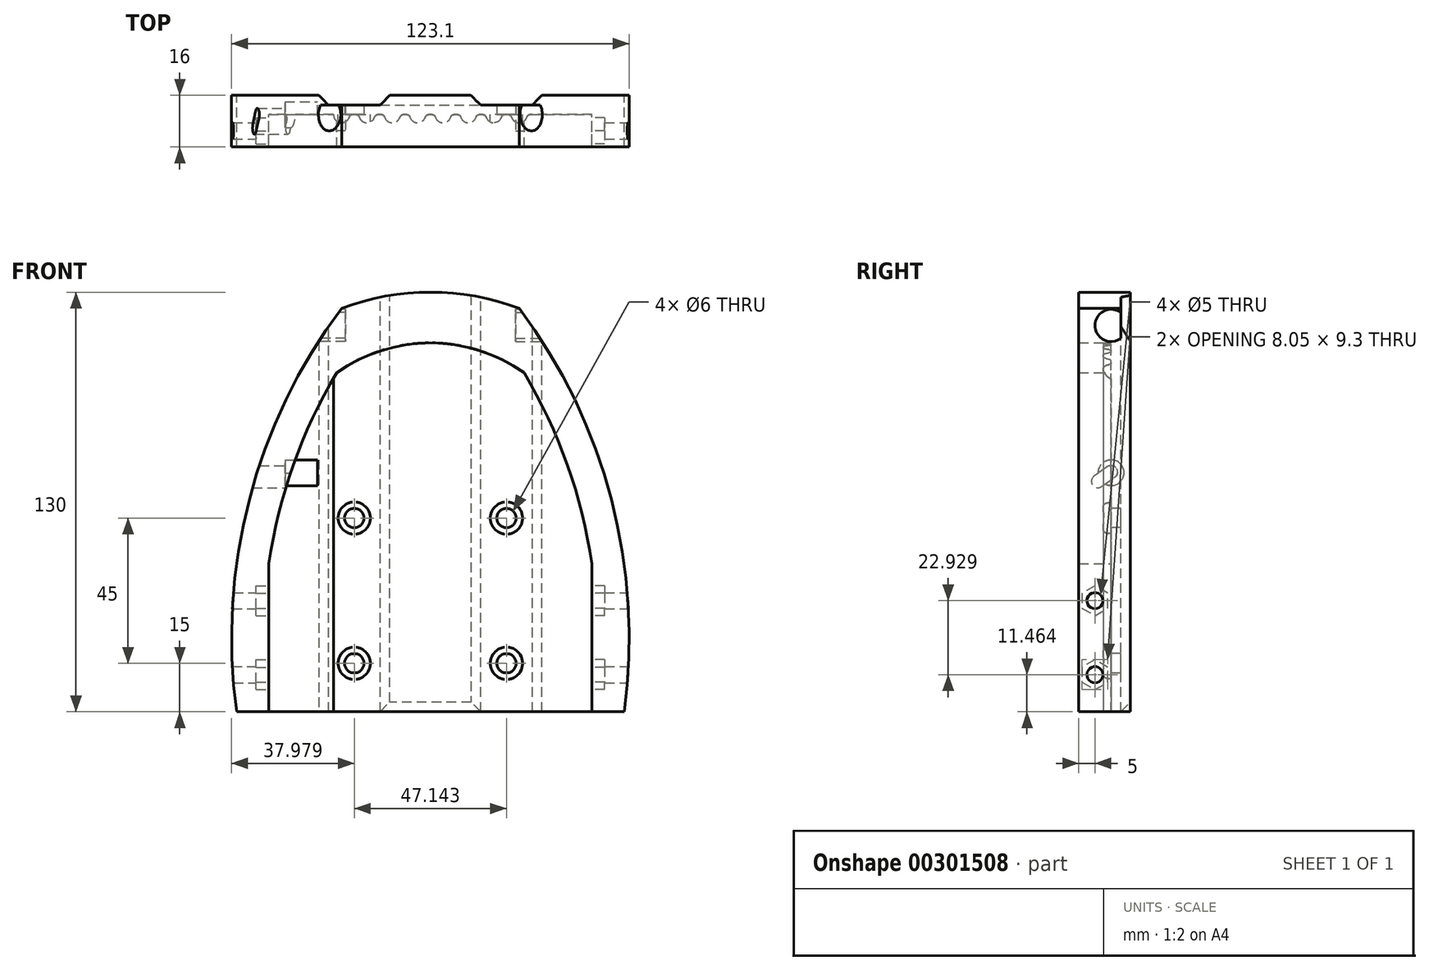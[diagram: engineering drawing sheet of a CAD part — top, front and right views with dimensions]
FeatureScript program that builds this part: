
annotation { "Feature Type Name" : "Feature", "Feature Type Description" : "" }
export const myFeature = defineFeature(function(context is Context, id is Id, definition is map)
    precondition{}
    {
        {
            var Q0;
            Q0=qCreatedBy(makeId("Front.planeOp"),FACE);
            var sketch = newSketch(context, id + "F0", { "sketchPlane" : qUnion([Q0])});
            skArc(sketch, "E0", {"start": v(-27.5, 125) * mm, "mid": v(-56.08, 65.7) * mm, "end": v(-60, 0) * mm});
            skArc(sketch, "E1", {"start": v(0, 130) * mm, "mid": v(-13.98, 128.74) * mm, "end": v(-27.5, 125) * mm});
            skLineSegment(sketch, "E2", {"start": v(-60, 0) * mm, "end": v(0, 0) * mm});
            skArc(sketch, "E3.MirrorCS", {"start": v(0, 130) * mm, "mid": v(13.98, 128.74) * mm, "end": v(27.5, 125) * mm});
            skArc(sketch, "E4.MirrorCS", {"start": v(27.5, 125) * mm, "mid": v(56.08, 65.7) * mm, "end": v(60, 0) * mm});
            skLineSegment(sketch, "E5.MirrorCS", {"start": v(60, 0) * mm, "end": v(0, 0) * mm});
            skSolve(sketch);
        }
        {
            var Q0;
            Q0=qSketchRegion(id+"F0",true);
            extrude(context, id + "F1", {"entities" : qUnion([Q0]), "depth" : 3 * mm});
        }
        {
            var Q0;
            Q0=makeQuery(id+"F1.opExtrude","CAP_FACE",FACE,{"disambiguationData":[OSD([sQuery(id+"F0.wireOp",EDGE,"E0"),sQuery(id+"F0.wireOp",EDGE,"E1"),sQuery(id+"F0.wireOp",EDGE,"E2"),sQuery(id+"F0.wireOp",EDGE,"E3.MirrorCS"),sQuery(id+"F0.wireOp",EDGE,"E4.MirrorCS"),sQuery(id+"F0.wireOp",EDGE,"E5.MirrorCS")])],"isStart":false});
            var sketch = newSketch(context, id + "F2", { "sketchPlane" : qUnion([Q0])});
            skArc(sketch, "E6", {"start": v(27.5, 125) * mm, "mid": v(0, 130) * mm, "end": v(-27.5, 125) * mm});
            skArc(sketch, "E7", {"start": v(-27.5, 125) * mm, "mid": v(-56.08, 65.7) * mm, "end": v(-60, 0) * mm});
            skArc(sketch, "E8", {"start": v(60, 0) * mm, "mid": v(56.08, 65.7) * mm, "end": v(27.5, 125) * mm});
            skArc(sketch, "E9", {"start": v(29.01, 105) * mm, "mid": v(0, 114.28) * mm, "end": v(-29.01, 105) * mm});
            skArc(sketch, "E10", {"start": v(-29.01, 105) * mm, "mid": v(-48.55, 54.3) * mm, "end": v(-50, 0) * mm});
            skArc(sketch, "E11", {"start": v(50, 0) * mm, "mid": v(48.55, 54.3) * mm, "end": v(29.01, 105) * mm});
            skLineSegment(sketch, "E12", {"start": v(-60, 0) * mm, "end": v(-50, 0) * mm});
            skLineSegment(sketch, "E13", {"start": v(50, 0) * mm, "end": v(60, 0) * mm});
            skLineSegment(sketch, "E14", {"start": v(-50, 45.86) * mm, "end": v(-50, 0) * mm});
            skPoint(sketch, "E15", {"position": v(-50, 43.93) * mm});
            skLineSegment(sketch, "E16.MirrorCS", {"start": v(50, 45.86) * mm, "end": v(50, 0) * mm});
            skSolve(sketch);
        }
        {
            var Q0;
            Q0=qSketchRegion(id+"F2",true);
            extrude(context, id + "F3", {"entities" : qUnion([Q0]), "operationType" : NewBodyOperationType.ADD, "depth" : 10 * mm});
        }
        {
            var Q0;
            Q0=makeQuery(id+"F1.opExtrude","SWEPT_FACE",FACE,{"disambiguationData":[OSD([sQuery(id+"F0.wireOp",EDGE,"E2"),sQuery(id+"F0.wireOp",EDGE,"E5.MirrorCS")])]});
            var sketch = newSketch(context, id + "F4", { "sketchPlane" : qUnion([Q0])});
            skArc(sketch, "E17", {"start": v(-25, 3) * mm, "mid": v(-27.5, 5.5) * mm, "end": v(-30, 3) * mm});
            skLineSegment(sketch, "E18", {"start": v(-30, 3) * mm, "end": v(-25, 3) * mm});
            skArc(sketch, "E19.1.0.0", {"start": v(-17.14, 3) * mm, "mid": v(-19.64, 5.5) * mm, "end": v(-22.14, 3) * mm});
            skLineSegment(sketch, "E19.1.0.1", {"start": v(-22.14, 3) * mm, "end": v(-17.14, 3) * mm});
            skArc(sketch, "E19.2.0.0", {"start": v(-9.29, 3) * mm, "mid": v(-11.79, 5.5) * mm, "end": v(-14.29, 3) * mm});
            skLineSegment(sketch, "E19.2.0.1", {"start": v(-14.29, 3) * mm, "end": v(-9.29, 3) * mm});
            skArc(sketch, "E19.3.0.0", {"start": v(-1.43, 3) * mm, "mid": v(-3.93, 5.5) * mm, "end": v(-6.43, 3) * mm});
            skLineSegment(sketch, "E19.3.0.1", {"start": v(-6.43, 3) * mm, "end": v(-1.43, 3) * mm});
            skArc(sketch, "E19.4.0.0", {"start": v(6.43, 3) * mm, "mid": v(3.93, 5.5) * mm, "end": v(1.43, 3) * mm});
            skLineSegment(sketch, "E19.4.0.1", {"start": v(1.43, 3) * mm, "end": v(6.43, 3) * mm});
            skArc(sketch, "E19.5.0.0", {"start": v(14.29, 3) * mm, "mid": v(11.79, 5.5) * mm, "end": v(9.29, 3) * mm});
            skLineSegment(sketch, "E19.5.0.1", {"start": v(9.29, 3) * mm, "end": v(14.29, 3) * mm});
            skArc(sketch, "E19.6.0.0", {"start": v(22.14, 3) * mm, "mid": v(19.64, 5.5) * mm, "end": v(17.14, 3) * mm});
            skLineSegment(sketch, "E19.6.0.1", {"start": v(17.14, 3) * mm, "end": v(22.14, 3) * mm});
            skArc(sketch, "E19.7.0.0", {"start": v(30, 3) * mm, "mid": v(27.5, 5.5) * mm, "end": v(25, 3) * mm});
            skLineSegment(sketch, "E19.7.0.1", {"start": v(25, 3) * mm, "end": v(30, 3) * mm});
            skLineSegment(sketch, "E19.direction1", {"start": v(-30, 3) * mm, "end": v(-22.14, 3) * mm, "construction": true});
            skSolve(sketch);
        }
        {
            var Q0;
            Q0=qSketchRegion(id+"F4",true);
            extrude(context, id + "F5", {"entities" : qUnion([Q0]), "operationType" : NewBodyOperationType.ADD, "endBound" : BoundingType.UP_TO_NEXT, "oppositeDirection" : true, "depth" : 25 * mm});
        }
        {
            var Q0;
            {var subQ0=sQuery(id+"F4.wireOp",EDGE,"E18");var subQ1=sQuery(id+"F4.wireOp",EDGE,"E17");var subQ2=sQuery(id+"F0.wireOp",EDGE,"E5.MirrorCS");var subQ3=sQuery(id+"F0.wireOp",EDGE,"E2");Q0=makeQuery(id+"F5.opExtrude","SWEPT_EDGE",EDGE,{"disambiguationData":[OSD([subQ3,subQ2,subQ1,subQ0]),TDD([makeQuery(id+"F4.imprint","INTERSECT",VERTEX,{"disambiguationData":[OD(1.0)],"derivedFrom":[makeQuery(id+"F1.opExtrude","CAP_EDGE",EDGE,{"disambiguationData":[OSD([subQ3,subQ2])],"isStart":false}),subQ1,subQ0]})])]});}
            var Q1;
            {var subQ0=sQuery(id+"F4.wireOp",EDGE,"E18");var subQ1=sQuery(id+"F4.wireOp",EDGE,"E17");var subQ2=sQuery(id+"F0.wireOp",EDGE,"E5.MirrorCS");var subQ3=sQuery(id+"F0.wireOp",EDGE,"E2");Q1=makeQuery(id+"F5.opExtrude","SWEPT_EDGE",EDGE,{"disambiguationData":[OSD([subQ3,subQ2,subQ1,subQ0]),TDD([makeQuery(id+"F4.imprint","INTERSECT",VERTEX,{"disambiguationData":[OD(0.0)],"derivedFrom":[makeQuery(id+"F1.opExtrude","CAP_EDGE",EDGE,{"disambiguationData":[OSD([subQ3,subQ2])],"isStart":false}),subQ1,subQ0]})])]});}
            var Q2;
            {var subQ0=sQuery(id+"F4.wireOp",EDGE,"E19.1.0.1");var subQ1=sQuery(id+"F4.wireOp",EDGE,"E19.1.0.0");var subQ2=sQuery(id+"F0.wireOp",EDGE,"E5.MirrorCS");var subQ3=sQuery(id+"F0.wireOp",EDGE,"E2");Q2=makeQuery(id+"F5.opExtrude","SWEPT_EDGE",EDGE,{"disambiguationData":[OSD([subQ3,subQ2,subQ1,subQ0]),TDD([makeQuery(id+"F4.imprint","INTERSECT",VERTEX,{"disambiguationData":[OD(0.0)],"derivedFrom":[makeQuery(id+"F1.opExtrude","CAP_EDGE",EDGE,{"disambiguationData":[OSD([subQ3,subQ2])],"isStart":false}),subQ1,subQ0]})])]});}
            var Q3;
            {var subQ0=sQuery(id+"F4.wireOp",EDGE,"E19.2.0.1");var subQ1=sQuery(id+"F4.wireOp",EDGE,"E19.2.0.0");var subQ2=sQuery(id+"F0.wireOp",EDGE,"E5.MirrorCS");var subQ3=sQuery(id+"F0.wireOp",EDGE,"E2");Q3=makeQuery(id+"F5.opExtrude","SWEPT_EDGE",EDGE,{"disambiguationData":[OSD([subQ3,subQ2,subQ1,subQ0]),TDD([makeQuery(id+"F4.imprint","INTERSECT",VERTEX,{"disambiguationData":[OD(0.0)],"derivedFrom":[makeQuery(id+"F1.opExtrude","CAP_EDGE",EDGE,{"disambiguationData":[OSD([subQ3,subQ2])],"isStart":false}),subQ1,subQ0]})])]});}
            var Q4;
            {var subQ0=sQuery(id+"F4.wireOp",EDGE,"E19.3.0.1");var subQ1=sQuery(id+"F4.wireOp",EDGE,"E19.3.0.0");var subQ2=sQuery(id+"F0.wireOp",EDGE,"E5.MirrorCS");var subQ3=sQuery(id+"F0.wireOp",EDGE,"E2");Q4=makeQuery(id+"F5.opExtrude","SWEPT_EDGE",EDGE,{"disambiguationData":[OSD([subQ3,subQ2,subQ1,subQ0]),TDD([makeQuery(id+"F4.imprint","INTERSECT",VERTEX,{"disambiguationData":[OD(0.0)],"derivedFrom":[makeQuery(id+"F1.opExtrude","CAP_EDGE",EDGE,{"disambiguationData":[OSD([subQ3,subQ2])],"isStart":false}),subQ1,subQ0]})])]});}
            var Q5;
            {var subQ0=sQuery(id+"F4.wireOp",EDGE,"E19.4.0.1");var subQ1=sQuery(id+"F4.wireOp",EDGE,"E19.4.0.0");var subQ2=sQuery(id+"F0.wireOp",EDGE,"E5.MirrorCS");var subQ3=sQuery(id+"F0.wireOp",EDGE,"E2");Q5=makeQuery(id+"F5.opExtrude","SWEPT_EDGE",EDGE,{"disambiguationData":[OSD([subQ3,subQ2,subQ1,subQ0]),TDD([makeQuery(id+"F4.imprint","INTERSECT",VERTEX,{"disambiguationData":[OD(0.0)],"derivedFrom":[makeQuery(id+"F1.opExtrude","CAP_EDGE",EDGE,{"disambiguationData":[OSD([subQ3,subQ2])],"isStart":false}),subQ1,subQ0]})])]});}
            var Q6;
            {var subQ0=sQuery(id+"F4.wireOp",EDGE,"E19.5.0.1");var subQ1=sQuery(id+"F4.wireOp",EDGE,"E19.5.0.0");var subQ2=sQuery(id+"F0.wireOp",EDGE,"E5.MirrorCS");var subQ3=sQuery(id+"F0.wireOp",EDGE,"E2");Q6=makeQuery(id+"F5.opExtrude","SWEPT_EDGE",EDGE,{"disambiguationData":[OSD([subQ3,subQ2,subQ1,subQ0]),TDD([makeQuery(id+"F4.imprint","INTERSECT",VERTEX,{"disambiguationData":[OD(0.0)],"derivedFrom":[makeQuery(id+"F1.opExtrude","CAP_EDGE",EDGE,{"disambiguationData":[OSD([subQ3,subQ2])],"isStart":false}),subQ1,subQ0]})])]});}
            var Q7;
            {var subQ0=sQuery(id+"F4.wireOp",EDGE,"E19.6.0.1");var subQ1=sQuery(id+"F4.wireOp",EDGE,"E19.6.0.0");var subQ2=sQuery(id+"F0.wireOp",EDGE,"E5.MirrorCS");var subQ3=sQuery(id+"F0.wireOp",EDGE,"E2");Q7=makeQuery(id+"F5.opExtrude","SWEPT_EDGE",EDGE,{"disambiguationData":[OSD([subQ3,subQ2,subQ1,subQ0]),TDD([makeQuery(id+"F4.imprint","INTERSECT",VERTEX,{"disambiguationData":[OD(0.0)],"derivedFrom":[makeQuery(id+"F1.opExtrude","CAP_EDGE",EDGE,{"disambiguationData":[OSD([subQ3,subQ2])],"isStart":false}),subQ1,subQ0]})])]});}
            var Q8;
            {var subQ0=sQuery(id+"F4.wireOp",EDGE,"E19.7.0.1");var subQ1=sQuery(id+"F4.wireOp",EDGE,"E19.7.0.0");var subQ2=sQuery(id+"F0.wireOp",EDGE,"E5.MirrorCS");var subQ3=sQuery(id+"F0.wireOp",EDGE,"E2");Q8=makeQuery(id+"F5.opExtrude","SWEPT_EDGE",EDGE,{"disambiguationData":[OSD([subQ3,subQ2,subQ1,subQ0]),TDD([makeQuery(id+"F4.imprint","INTERSECT",VERTEX,{"disambiguationData":[OD(0.0)],"derivedFrom":[makeQuery(id+"F1.opExtrude","CAP_EDGE",EDGE,{"disambiguationData":[OSD([subQ3,subQ2])],"isStart":false}),subQ1,subQ0]})])]});}
            var Q9;
            {var subQ0=sQuery(id+"F4.wireOp",EDGE,"E19.8.0.1");var subQ1=sQuery(id+"F4.wireOp",EDGE,"E19.8.0.0");var subQ2=sQuery(id+"F0.wireOp",EDGE,"E5.MirrorCS");var subQ3=sQuery(id+"F0.wireOp",EDGE,"E2");Q9=makeQuery(id+"F5.opExtrude","SWEPT_EDGE",EDGE,{"disambiguationData":[OSD([subQ3,subQ2,subQ1,subQ0]),TDD([makeQuery(id+"F4.imprint","INTERSECT",VERTEX,{"disambiguationData":[OD(0.0)],"derivedFrom":[makeQuery(id+"F1.opExtrude","CAP_EDGE",EDGE,{"disambiguationData":[OSD([subQ3,subQ2])],"isStart":false}),subQ1,subQ0]})])]});}
            var Q10;
            {var subQ0=sQuery(id+"F4.wireOp",EDGE,"E19.9.0.1");var subQ1=sQuery(id+"F4.wireOp",EDGE,"E19.9.0.0");var subQ2=sQuery(id+"F0.wireOp",EDGE,"E5.MirrorCS");var subQ3=sQuery(id+"F0.wireOp",EDGE,"E2");Q10=makeQuery(id+"F5.opExtrude","SWEPT_EDGE",EDGE,{"disambiguationData":[OSD([subQ3,subQ2,subQ1,subQ0]),TDD([makeQuery(id+"F4.imprint","INTERSECT",VERTEX,{"disambiguationData":[OD(0.0)],"derivedFrom":[makeQuery(id+"F1.opExtrude","CAP_EDGE",EDGE,{"disambiguationData":[OSD([subQ3,subQ2])],"isStart":false}),subQ1,subQ0]})])]});}
            var Q11;
            {var subQ0=sQuery(id+"F4.wireOp",EDGE,"E19.1.0.1");var subQ1=sQuery(id+"F4.wireOp",EDGE,"E19.1.0.0");var subQ2=sQuery(id+"F0.wireOp",EDGE,"E5.MirrorCS");var subQ3=sQuery(id+"F0.wireOp",EDGE,"E2");Q11=makeQuery(id+"F5.opExtrude","SWEPT_EDGE",EDGE,{"disambiguationData":[OSD([subQ3,subQ2,subQ1,subQ0]),TDD([makeQuery(id+"F4.imprint","INTERSECT",VERTEX,{"disambiguationData":[OD(1.0)],"derivedFrom":[makeQuery(id+"F1.opExtrude","CAP_EDGE",EDGE,{"disambiguationData":[OSD([subQ3,subQ2])],"isStart":false}),subQ1,subQ0]})])]});}
            var Q12;
            {var subQ0=sQuery(id+"F4.wireOp",EDGE,"E19.2.0.1");var subQ1=sQuery(id+"F4.wireOp",EDGE,"E19.2.0.0");var subQ2=sQuery(id+"F0.wireOp",EDGE,"E5.MirrorCS");var subQ3=sQuery(id+"F0.wireOp",EDGE,"E2");Q12=makeQuery(id+"F5.opExtrude","SWEPT_EDGE",EDGE,{"disambiguationData":[OSD([subQ3,subQ2,subQ1,subQ0]),TDD([makeQuery(id+"F4.imprint","INTERSECT",VERTEX,{"disambiguationData":[OD(1.0)],"derivedFrom":[makeQuery(id+"F1.opExtrude","CAP_EDGE",EDGE,{"disambiguationData":[OSD([subQ3,subQ2])],"isStart":false}),subQ1,subQ0]})])]});}
            var Q13;
            {var subQ0=sQuery(id+"F4.wireOp",EDGE,"E19.3.0.1");var subQ1=sQuery(id+"F4.wireOp",EDGE,"E19.3.0.0");var subQ2=sQuery(id+"F0.wireOp",EDGE,"E5.MirrorCS");var subQ3=sQuery(id+"F0.wireOp",EDGE,"E2");Q13=makeQuery(id+"F5.opExtrude","SWEPT_EDGE",EDGE,{"disambiguationData":[OSD([subQ3,subQ2,subQ1,subQ0]),TDD([makeQuery(id+"F4.imprint","INTERSECT",VERTEX,{"disambiguationData":[OD(1.0)],"derivedFrom":[makeQuery(id+"F1.opExtrude","CAP_EDGE",EDGE,{"disambiguationData":[OSD([subQ3,subQ2])],"isStart":false}),subQ1,subQ0]})])]});}
            var Q14;
            {var subQ0=sQuery(id+"F4.wireOp",EDGE,"E19.4.0.1");var subQ1=sQuery(id+"F4.wireOp",EDGE,"E19.4.0.0");var subQ2=sQuery(id+"F0.wireOp",EDGE,"E5.MirrorCS");var subQ3=sQuery(id+"F0.wireOp",EDGE,"E2");Q14=makeQuery(id+"F5.opExtrude","SWEPT_EDGE",EDGE,{"disambiguationData":[OSD([subQ3,subQ2,subQ1,subQ0]),TDD([makeQuery(id+"F4.imprint","INTERSECT",VERTEX,{"disambiguationData":[OD(1.0)],"derivedFrom":[makeQuery(id+"F1.opExtrude","CAP_EDGE",EDGE,{"disambiguationData":[OSD([subQ3,subQ2])],"isStart":false}),subQ1,subQ0]})])]});}
            var Q15;
            {var subQ0=sQuery(id+"F4.wireOp",EDGE,"E19.5.0.1");var subQ1=sQuery(id+"F4.wireOp",EDGE,"E19.5.0.0");var subQ2=sQuery(id+"F0.wireOp",EDGE,"E5.MirrorCS");var subQ3=sQuery(id+"F0.wireOp",EDGE,"E2");Q15=makeQuery(id+"F5.opExtrude","SWEPT_EDGE",EDGE,{"disambiguationData":[OSD([subQ3,subQ2,subQ1,subQ0]),TDD([makeQuery(id+"F4.imprint","INTERSECT",VERTEX,{"disambiguationData":[OD(1.0)],"derivedFrom":[makeQuery(id+"F1.opExtrude","CAP_EDGE",EDGE,{"disambiguationData":[OSD([subQ3,subQ2])],"isStart":false}),subQ1,subQ0]})])]});}
            var Q16;
            {var subQ0=sQuery(id+"F4.wireOp",EDGE,"E19.6.0.1");var subQ1=sQuery(id+"F4.wireOp",EDGE,"E19.6.0.0");var subQ2=sQuery(id+"F0.wireOp",EDGE,"E5.MirrorCS");var subQ3=sQuery(id+"F0.wireOp",EDGE,"E2");Q16=makeQuery(id+"F5.opExtrude","SWEPT_EDGE",EDGE,{"disambiguationData":[OSD([subQ3,subQ2,subQ1,subQ0]),TDD([makeQuery(id+"F4.imprint","INTERSECT",VERTEX,{"disambiguationData":[OD(1.0)],"derivedFrom":[makeQuery(id+"F1.opExtrude","CAP_EDGE",EDGE,{"disambiguationData":[OSD([subQ3,subQ2])],"isStart":false}),subQ1,subQ0]})])]});}
            var Q17;
            {var subQ0=sQuery(id+"F4.wireOp",EDGE,"E19.7.0.1");var subQ1=sQuery(id+"F4.wireOp",EDGE,"E19.7.0.0");var subQ2=sQuery(id+"F0.wireOp",EDGE,"E5.MirrorCS");var subQ3=sQuery(id+"F0.wireOp",EDGE,"E2");Q17=makeQuery(id+"F5.opExtrude","SWEPT_EDGE",EDGE,{"disambiguationData":[OSD([subQ3,subQ2,subQ1,subQ0]),TDD([makeQuery(id+"F4.imprint","INTERSECT",VERTEX,{"disambiguationData":[OD(1.0)],"derivedFrom":[makeQuery(id+"F1.opExtrude","CAP_EDGE",EDGE,{"disambiguationData":[OSD([subQ3,subQ2])],"isStart":false}),subQ1,subQ0]})])]});}
            var Q18;
            {var subQ0=sQuery(id+"F4.wireOp",EDGE,"E19.8.0.1");var subQ1=sQuery(id+"F4.wireOp",EDGE,"E19.8.0.0");var subQ2=sQuery(id+"F0.wireOp",EDGE,"E5.MirrorCS");var subQ3=sQuery(id+"F0.wireOp",EDGE,"E2");Q18=makeQuery(id+"F5.opExtrude","SWEPT_EDGE",EDGE,{"disambiguationData":[OSD([subQ3,subQ2,subQ1,subQ0]),TDD([makeQuery(id+"F4.imprint","INTERSECT",VERTEX,{"disambiguationData":[OD(1.0)],"derivedFrom":[makeQuery(id+"F1.opExtrude","CAP_EDGE",EDGE,{"disambiguationData":[OSD([subQ3,subQ2])],"isStart":false}),subQ1,subQ0]})])]});}
            var Q19;
            {var subQ0=sQuery(id+"F4.wireOp",EDGE,"E19.9.0.1");var subQ1=sQuery(id+"F4.wireOp",EDGE,"E19.9.0.0");var subQ2=sQuery(id+"F0.wireOp",EDGE,"E5.MirrorCS");var subQ3=sQuery(id+"F0.wireOp",EDGE,"E2");Q19=makeQuery(id+"F5.opExtrude","SWEPT_EDGE",EDGE,{"disambiguationData":[OSD([subQ3,subQ2,subQ1,subQ0]),TDD([makeQuery(id+"F4.imprint","INTERSECT",VERTEX,{"disambiguationData":[OD(1.0)],"derivedFrom":[makeQuery(id+"F1.opExtrude","CAP_EDGE",EDGE,{"disambiguationData":[OSD([subQ3,subQ2])],"isStart":false}),subQ1,subQ0]})])]});}
            fillet(context, id + "F6", {"entities" : qUnion([Q0, Q1, Q2, Q3, Q4, Q5, Q6, Q7, Q8, Q9, Q10, Q11, Q12, Q13, Q14, Q15, Q16, Q17, Q18, Q19]), "radius" : 1 * mm, "tangentPropagation" : true, "allowEdgeOverflow" : false});
        }
        {
            var Q0;
            Q0=makeQuery(id+"F3.opExtrude","CAP_FACE",FACE,{"disambiguationData":[OSD([sQuery(id+"F2.wireOp",EDGE,"E6"),sQuery(id+"F2.wireOp",EDGE,"E7"),sQuery(id+"F2.wireOp",EDGE,"E8"),sQuery(id+"F2.wireOp",EDGE,"E9"),sQuery(id+"F2.wireOp",EDGE,"E10"),sQuery(id+"F2.wireOp",EDGE,"E11"),sQuery(id+"F2.wireOp",EDGE,"E12"),sQuery(id+"F2.wireOp",EDGE,"E13")])],"isStart":false});
            var sketch = newSketch(context, id + "F7", { "sketchPlane" : qUnion([Q0])});
            skPoint(sketch, "E20", {"position": v(-31.34, 119.68) * mm});
            skPoint(sketch, "E21", {"position": v(31.34, 119.68) * mm});
            skSolve(sketch);
        }
        {
            var Q0;
            Q0=qCreatedBy(makeId("Right.planeOp"),FACE);
            cPlane(context, id + "F8", {"entities" : qUnion([Q0]), "cplaneType" : CPlaneType.OFFSET, "offset" : (62.67 / 2) * mm, "width" : 150 * mm, "height" : 150 * mm});
        }
        {
            var Q0;
            Q0=qCreatedBy(makeId("Right.planeOp"),FACE);
            cPlane(context, id + "F9", {"entities" : qUnion([Q0]), "cplaneType" : CPlaneType.OFFSET, "offset" : (62.67 / 2) * mm, "oppositeDirection" : true, "width" : 150 * mm, "height" : 150 * mm});
        }
        {
            var Q0;
            Q0=qCreatedBy(id+"F8.planeOp",FACE);
            var sketch = newSketch(context, id + "F10", { "sketchPlane" : qUnion([Q0])});
            skCircle(sketch, "E22", {"center": v(-3, 119.68) * mm, "radius": 5 * mm});
            skSolve(sketch);
        }
        {
            var Q0;
            Q0=qSketchRegion(id+"F10",true);
            extrude(context, id + "F11", {"entities" : qUnion([Q0]), "operationType" : NewBodyOperationType.REMOVE, "oppositeDirection" : true, "depth" : 5 * mm, "hasSecondDirection" : true, "secondDirectionOppositeDirection" : false, "secondDirectionDepth" : 25 * mm});
        }
        {
            var Q0;
            Q0=qCreatedBy(id+"F9.planeOp",FACE);
            var sketch = newSketch(context, id + "F12", { "sketchPlane" : qUnion([Q0])});
            skCircle(sketch, "E23", {"center": v(-3, 119.68) * mm, "radius": 5 * mm});
            skSolve(sketch);
        }
        {
            var Q0;
            Q0=qSketchRegion(id+"F12",true);
            extrude(context, id + "F13", {"entities" : qUnion([Q0]), "operationType" : NewBodyOperationType.REMOVE, "depth" : 5 * mm, "hasSecondDirection" : true, "secondDirectionOppositeDirection" : true, "secondDirectionDepth" : 25 * mm});
        }
        {
            var Q0;
            {var subQ0=makeQuery(id+"F5.opExtrude","CAP_FACE",FACE,{"disambiguationData":[OSD([sQuery(id+"F4.wireOp",EDGE,"E19.5.0.0"),sQuery(id+"F4.wireOp",EDGE,"E19.5.0.1")])],"isStart":true});var subQ1=sQuery(id+"F0.wireOp",EDGE,"E5.MirrorCS");var subQ2=sQuery(id+"F0.wireOp",EDGE,"E2");var subQ3=makeQuery(id+"F1.opExtrude","SWEPT_FACE",FACE,{"disambiguationData":[OSD([subQ2,subQ1])]});var subQ4=sQuery(id+"F4.wireOp",EDGE,"E19.3.0.0");var subQ5=makeQuery(id+"F5.opExtrude","CAP_FACE",FACE,{"disambiguationData":[OSD([subQ4,sQuery(id+"F4.wireOp",EDGE,"E19.3.0.1")])],"isStart":true});var subQ6=sQuery(id+"F4.wireOp",EDGE,"E19.2.0.0");var subQ7=makeQuery(id+"F5.opExtrude","CAP_FACE",FACE,{"disambiguationData":[OSD([subQ6,sQuery(id+"F4.wireOp",EDGE,"E19.2.0.1")])],"isStart":true});var subQ8=makeQuery(id+"F5.opExtrude","SWEPT_FACE",FACE,{"disambiguationData":[OSD([subQ6])]});var subQ9=sQuery(id+"F4.wireOp",EDGE,"E19.1.0.0");var subQ10=makeQuery(id+"F5.opExtrude","CAP_FACE",FACE,{"disambiguationData":[OSD([subQ9,sQuery(id+"F4.wireOp",EDGE,"E19.1.0.1")])],"isStart":true});var subQ11=makeQuery(id+"F5.opExtrude","CAP_FACE",FACE,{"disambiguationData":[OSD([sQuery(id+"F4.wireOp",EDGE,"E19.4.0.0"),sQuery(id+"F4.wireOp",EDGE,"E19.4.0.1")])],"isStart":true});var subQ12=makeQuery(id+"F3.opExtrude","SWEPT_FACE",FACE,{"disambiguationData":[OSD([sQuery(id+"F2.wireOp",EDGE,"E9")])]});var subQ13=sQuery(id+"F4.wireOp",EDGE,"E17");var subQ14=makeQuery(id+"F5.opExtrude","CAP_FACE",FACE,{"disambiguationData":[OSD([subQ13,sQuery(id+"F4.wireOp",EDGE,"E18")])],"isStart":true});var subQ15=makeQuery(id+"F5.opExtrude","CAP_FACE",FACE,{"disambiguationData":[OSD([sQuery(id+"F4.wireOp",EDGE,"E19.6.0.0"),sQuery(id+"F4.wireOp",EDGE,"E19.6.0.1")])],"isStart":true});var subQ16=makeQuery(id+"F5.opExtrude","CAP_FACE",FACE,{"disambiguationData":[OSD([sQuery(id+"F4.wireOp",EDGE,"E19.7.0.0"),sQuery(id+"F4.wireOp",EDGE,"E19.7.0.1")])],"isStart":true});var subQ17=makeQuery(id+"F5.opExtrude","CAP_FACE",FACE,{"disambiguationData":[OSD([sQuery(id+"F4.wireOp",EDGE,"E19.8.0.0"),sQuery(id+"F4.wireOp",EDGE,"E19.8.0.1")])],"isStart":true});var subQ18=makeQuery(id+"F5.opExtrude","CAP_FACE",FACE,{"disambiguationData":[OSD([sQuery(id+"F4.wireOp",EDGE,"E19.9.0.0"),sQuery(id+"F4.wireOp",EDGE,"E19.9.0.1")])],"isStart":true});var subQ19=makeQuery(id+"F1.opExtrude","CAP_FACE",FACE,{"disambiguationData":[OSD([sQuery(id+"F0.wireOp",EDGE,"E0"),sQuery(id+"F0.wireOp",EDGE,"E1"),subQ2,sQuery(id+"F0.wireOp",EDGE,"E3.MirrorCS"),sQuery(id+"F0.wireOp",EDGE,"E4.MirrorCS"),subQ1])],"isStart":false});var subQ20=makeQuery(id+"F5.opExtrude","SWEPT_FACE",FACE,{"disambiguationData":[OSD([subQ9])]});Q0=makeQuery(id+"FagDk5R1PXxC9WP_1.boolean.opBoolean","MERGE",FACE,{"derivedFrom":[makeQuery(id+"F5.boolean.opBoolean","SPLIT",FACE,{"disambiguationData":[TD([subQ3,subQ12,makeQuery(id+"F5.opExtrude","SWEPT_FACE",FACE,{"disambiguationData":[OSD([subQ13])]}),subQ14,subQ20,subQ10,subQ7,subQ5,subQ11,subQ0,subQ15,subQ16,subQ17,subQ18])],"derivedFrom":subQ19}),makeQuery(id+"F5.boolean.opBoolean","SPLIT",FACE,{"disambiguationData":[TD([subQ3,subQ12,subQ14,subQ20,subQ10,subQ8,subQ7,subQ5,subQ11,subQ0,subQ15,subQ16,subQ17,subQ18])],"derivedFrom":subQ19}),makeQuery(id+"F5.boolean.opBoolean","SPLIT",FACE,{"disambiguationData":[TD([subQ3,subQ12,subQ14,subQ10,subQ8,subQ7,makeQuery(id+"F5.opExtrude","SWEPT_FACE",FACE,{"disambiguationData":[OSD([subQ4])]}),subQ5,subQ11,subQ0,subQ15,subQ16,subQ17,subQ18])],"derivedFrom":subQ19}),makeQuery(id+"FagDk5R1PXxC9WP_1.opExtrude","SWEPT_FACE",FACE,{"disambiguationData":[OSD([sQuery(id+"FtMZI0YXXD80vIJ_1.wireOp",EDGE,"6BlepP5m-DG3n-HtGD-IaAT-YB7duayLEJRe.bottom")])]})]});}
            var sketch = newSketch(context, id + "F14", { "sketchPlane" : qUnion([Q0])});
            skCircle(sketch, "E24", {"center": v(-23.57, 15) * mm, "radius": 3 * mm});
            skPoint(sketch, "E24.centerSnap0", {"position": v(-23.57, 0) * mm});
            skCircle(sketch, "E25", {"center": v(-23.57, 60) * mm, "radius": 3 * mm});
            skCircle(sketch, "E26.MirrorC", {"center": v(23.57, 15) * mm, "radius": 3 * mm});
            skCircle(sketch, "E27.MirrorC", {"center": v(23.57, 60) * mm, "radius": 3 * mm});
            skPoint(sketch, "E28", {"position": v(0, 0) * mm});
            skSolve(sketch);
        }
        {
            var Q0;
            Q0=qSketchRegion(id+"F14",true);
            extrude(context, id + "F15", {"entities" : qUnion([Q0]), "operationType" : NewBodyOperationType.REMOVE, "oppositeDirection" : true, "depth" : 25 * mm});
        }
        {
            var Q0;
            {var subQ0=sQuery(id+"F4.wireOp",EDGE,"E17");var subQ1=makeQuery(id+"F3.opExtrude","SWEPT_FACE",FACE,{"disambiguationData":[OSD([sQuery(id+"F2.wireOp",EDGE,"E10")])]});var subQ2=makeQuery(id+"F3.opExtrude","SWEPT_FACE",FACE,{"disambiguationData":[OSD([sQuery(id+"F2.wireOp",EDGE,"E7")])]});var subQ3=sQuery(id+"F0.wireOp",EDGE,"E5.MirrorCS");var subQ4=sQuery(id+"F0.wireOp",EDGE,"E2");var subQ5=sQuery(id+"F0.wireOp",EDGE,"E0");var subQ6=makeQuery(id+"F1.opExtrude","CAP_FACE",FACE,{"disambiguationData":[OSD([subQ5,sQuery(id+"F0.wireOp",EDGE,"E1"),subQ4,sQuery(id+"F0.wireOp",EDGE,"E3.MirrorCS"),sQuery(id+"F0.wireOp",EDGE,"E4.MirrorCS"),subQ3])],"isStart":false});var subQ7=makeQuery(id+"F1.opExtrude","SWEPT_FACE",FACE,{"disambiguationData":[OSD([subQ5])]});Q0=makeQuery(id+"F5.boolean.opBoolean","SPLIT",FACE,{"disambiguationData":[TD([subQ7,makeQuery(id+"F1.opExtrude","SWEPT_FACE",FACE,{"disambiguationData":[OSD([subQ4,subQ3])]}),subQ2,subQ1,makeQuery(id+"FEmyDYQQVgRQXe1_1.boolean.opBoolean","COPY",FACE,{"disambiguationData":[TD([subQ7])],"derivedFrom":makeQuery(id+"FEmyDYQQVgRQXe1_1.opExtrude","SWEPT_FACE",FACE,{"disambiguationData":[OSD([sQuery(id+"F95mhF6FaMZOlkV_1.wireOp",EDGE,"16wo293t-KL3b-4ck3-VDR1-H0NEiYk0Jyv5")])]})}),makeQuery(id+"F5.opExtrude","SWEPT_FACE",FACE,{"disambiguationData":[OSD([subQ0])]}),makeQuery(id+"F5.opExtrude","CAP_FACE",FACE,{"disambiguationData":[OSD([subQ0,sQuery(id+"F4.wireOp",EDGE,"E18")])],"isStart":true}),makeQuery(id+"F5.opExtrude","CAP_FACE",FACE,{"disambiguationData":[OSD([sQuery(id+"F4.wireOp",EDGE,"E19.1.0.0"),sQuery(id+"F4.wireOp",EDGE,"E19.1.0.1")])],"isStart":true}),makeQuery(id+"F5.opExtrude","CAP_FACE",FACE,{"disambiguationData":[OSD([sQuery(id+"F4.wireOp",EDGE,"E19.2.0.0"),sQuery(id+"F4.wireOp",EDGE,"E19.2.0.1")])],"isStart":true}),makeQuery(id+"F5.opExtrude","CAP_FACE",FACE,{"disambiguationData":[OSD([sQuery(id+"F4.wireOp",EDGE,"E19.3.0.0"),sQuery(id+"F4.wireOp",EDGE,"E19.3.0.1")])],"isStart":true}),makeQuery(id+"F5.opExtrude","CAP_FACE",FACE,{"disambiguationData":[OSD([sQuery(id+"F4.wireOp",EDGE,"E19.4.0.0"),sQuery(id+"F4.wireOp",EDGE,"E19.4.0.1")])],"isStart":true}),makeQuery(id+"F5.opExtrude","CAP_FACE",FACE,{"disambiguationData":[OSD([sQuery(id+"F4.wireOp",EDGE,"E19.5.0.0"),sQuery(id+"F4.wireOp",EDGE,"E19.5.0.1")])],"isStart":true}),makeQuery(id+"F5.opExtrude","CAP_FACE",FACE,{"disambiguationData":[OSD([sQuery(id+"F4.wireOp",EDGE,"E19.6.0.0"),sQuery(id+"F4.wireOp",EDGE,"E19.6.0.1")])],"isStart":true}),makeQuery(id+"F5.opExtrude","CAP_FACE",FACE,{"disambiguationData":[OSD([sQuery(id+"F4.wireOp",EDGE,"E19.7.0.0"),sQuery(id+"F4.wireOp",EDGE,"E19.7.0.1")])],"isStart":true}),makeQuery(id+"F5.opExtrude","CAP_FACE",FACE,{"disambiguationData":[OSD([sQuery(id+"F4.wireOp",EDGE,"E19.8.0.0"),sQuery(id+"F4.wireOp",EDGE,"E19.8.0.1")])],"isStart":true}),makeQuery(id+"F5.opExtrude","CAP_FACE",FACE,{"disambiguationData":[OSD([sQuery(id+"F4.wireOp",EDGE,"E19.9.0.0"),sQuery(id+"F4.wireOp",EDGE,"E19.9.0.1")])],"isStart":true})])],"derivedFrom":subQ6});}
            var sketch = newSketch(context, id + "F16", { "sketchPlane" : qUnion([Q0])});
            skCircle(sketch, "E29", {"center": v(23.57, 60) * mm, "radius": 5 * mm});
            skCircle(sketch, "E30", {"center": v(-23.57, 60) * mm, "radius": 5 * mm});
            skCircle(sketch, "E31", {"center": v(-23.57, 15) * mm, "radius": 5 * mm});
            skCircle(sketch, "E32", {"center": v(23.57, 15) * mm, "radius": 5 * mm});
            skSolve(sketch);
        }
        {
            var Q0;
            Q0=qSketchRegion(id+"F16",true);
            extrude(context, id + "F17", {"entities" : qUnion([Q0]), "operationType" : NewBodyOperationType.REMOVE, "depth" : 25 * mm});
        }
        {
            var Q0;
            Q0=makeQuery(id+"F1.opExtrude","CAP_FACE",FACE,{"disambiguationData":[OSD([sQuery(id+"F0.wireOp",EDGE,"E0"),sQuery(id+"F0.wireOp",EDGE,"E1"),sQuery(id+"F0.wireOp",EDGE,"E2"),sQuery(id+"F0.wireOp",EDGE,"E3.MirrorCS"),sQuery(id+"F0.wireOp",EDGE,"E4.MirrorCS"),sQuery(id+"F0.wireOp",EDGE,"E5.MirrorCS")])],"isStart":true});
            var sketch = newSketch(context, id + "F18", { "sketchPlane" : qUnion([Q0])});
            skLineSegment(sketch, "E33.left", {"start": v(15.57, 0) * mm, "end": v(15.57, 128.43) * mm});
            skLineSegment(sketch, "E33.right", {"start": v(-15.57, 0) * mm, "end": v(-15.57, 128.43) * mm});
            skPoint(sketch, "E34", {"position": v(23.57, 15) * mm});
            skPoint(sketch, "E35", {"position": v(-23.57, 15) * mm});
            skArc(sketch, "E36", {"start": v(15.57, 128.43) * mm, "mid": v(0, 130) * mm, "end": v(-15.57, 128.43) * mm});
            skArc(sketch, "E37", {"start": v(60, 0) * mm, "mid": v(56.93, 62.32) * mm, "end": v(31.57, 119.34) * mm});
            skLineSegment(sketch, "E38", {"start": v(60, 0) * mm, "end": v(31.57, 0) * mm});
            skLineSegment(sketch, "E39", {"start": v(31.57, 0) * mm, "end": v(31.57, 119.34) * mm});
            skLineSegment(sketch, "E40.MirrorCS", {"start": v(-60, 0) * mm, "end": v(-31.57, 0) * mm});
            skArc(sketch, "E41.MirrorCS", {"start": v(-60, 0) * mm, "mid": v(-56.93, 62.32) * mm, "end": v(-31.57, 119.34) * mm});
            skLineSegment(sketch, "E42.MirrorCS", {"start": v(-31.57, 0) * mm, "end": v(-31.57, 119.34) * mm});
            skLineSegment(sketch, "E43", {"start": v(-15.57, 0) * mm, "end": v(15.57, 0) * mm});
            skPoint(sketch, "E44", {"position": v(0, 0) * mm});
            skSolve(sketch);
        }
        {
            var Q0;
            Q0=qSketchRegion(id+"F18",true);
            extrude(context, id + "F19", {"entities" : qUnion([Q0]), "operationType" : NewBodyOperationType.ADD, "depth" : 3 * mm});
        }
        {
            var Q0;
            Q0=makeQuery(id+"F19.opExtrude","CAP_EDGE",EDGE,{"disambiguationData":[OSD([sQuery(id+"F18.wireOp",EDGE,"E33.left")])],"isStart":false});
            var Q1;
            Q1=makeQuery(id+"F19.opExtrude","CAP_EDGE",EDGE,{"disambiguationData":[OSD([sQuery(id+"F18.wireOp",EDGE,"E33.right")])],"isStart":false});
            var Q2;
            Q2=makeQuery(id+"F19.opExtrude","CAP_EDGE",EDGE,{"disambiguationData":[OSD([sQuery(id+"F18.wireOp",EDGE,"E42.MirrorCS")])],"isStart":false});
            var Q3;
            Q3=makeQuery(id+"F19.opExtrude","CAP_EDGE",EDGE,{"disambiguationData":[OSD([sQuery(id+"F18.wireOp",EDGE,"E39")])],"isStart":false});
            var Q4;
            Q4=makeQuery(id+"F19.opExtrude","CAP_EDGE",EDGE,{"disambiguationData":[OSD([sQuery(id+"F18.wireOp",EDGE,"zS66gYXZ-0WJ1-GNRd-CW5H-YCuno0UtB482")])],"isStart":false});
            var Q5;
            Q5=makeQuery(id+"F19.opExtrude","CAP_EDGE",EDGE,{"disambiguationData":[OSD([sQuery(id+"F18.wireOp",EDGE,"E43")])],"isStart":false});
            var Q6;
            Q6=makeQuery(id+"F19.opExtrude","CAP_EDGE",EDGE,{"disambiguationData":[OSD([sQuery(id+"F18.wireOp",EDGE,"6rLx0d4R-H4u5-pnFk-er2m-jyyjp0cNVsxB")])],"isStart":false});
            chamfer(context, id + "F20", {"entities" : qUnion([Q0, Q1, Q2, Q3, Q4, Q5, Q6]), "width" : 3 * mm, "tangentPropagation" : true});
        }
        {
            var Q0;
            Q0=makeQuery(id+"F3.opExtrude","SWEPT_FACE",FACE,{"disambiguationData":[OSD([sQuery(id+"F2.wireOp",EDGE,"E14")])]});
            var sketch = newSketch(context, id + "F21", { "sketchPlane" : qUnion([Q0])});
            skCircle(sketch, "E45", {"center": v(-8, 11.46) * mm, "radius": 2.5 * mm});
            skCircle(sketch, "E46", {"center": v(-8, 34.4) * mm, "radius": 2.5 * mm});
            skLineSegment(sketch, "E47", {"start": v(-13, 0) * mm, "end": v(-13, 22.93) * mm});
            skLineSegment(sketch, "E48", {"start": v(-13, 22.93) * mm, "end": v(-13, 45.86) * mm});
            skPoint(sketch, "E49", {"position": v(-13, 11.46) * mm});
            skPoint(sketch, "E50", {"position": v(-13, 34.4) * mm});
            skSolve(sketch);
        }
        {
            var Q0;
            Q0=qSketchRegion(id+"F21",true);
            extrude(context, id + "F22", {"entities" : qUnion([Q0]), "operationType" : NewBodyOperationType.REMOVE, "oppositeDirection" : true, "depth" : 25 * mm, "hasSecondDirection" : true, "secondDirectionBound" : SecondDirectionBoundingType.THROUGH_ALL, "secondDirectionOppositeDirection" : false, "secondDirectionDepth" : 25 * mm});
        }
        {
            var Q0;
            Q0=makeQuery(id+"F3.opExtrude","SWEPT_FACE",FACE,{"disambiguationData":[OSD([sQuery(id+"F2.wireOp",EDGE,"E14")])]});
            var sketch = newSketch(context, id + "F23", { "sketchPlane" : qUnion([Q0])});
            skCircle(sketch, "E51.cCircle", {"center": v(-8, 11.46) * mm, "radius": 4.03 * mm, "construction": true});
            skLineSegment(sketch, "E51.0", {"start": v(-12.03, 13.79) * mm, "end": v(-8, 16.11) * mm});
            skLineSegment(sketch, "E51.1", {"start": v(-8, 16.11) * mm, "end": v(-3.98, 13.79) * mm});
            skLineSegment(sketch, "E51.2", {"start": v(-3.97, 13.79) * mm, "end": v(-3.97, 9.14) * mm});
            skLineSegment(sketch, "E51.3", {"start": v(-3.97, 9.14) * mm, "end": v(-8, 6.82) * mm});
            skLineSegment(sketch, "E51.4", {"start": v(-8, 6.82) * mm, "end": v(-12.03, 9.14) * mm});
            skLineSegment(sketch, "E51.5", {"start": v(-12.02, 9.14) * mm, "end": v(-12.02, 13.79) * mm});
            skPoint(sketch, "E51.0.midPoint", {"position": v(-10.01, 14.95) * mm});
            skCircle(sketch, "E52.cCircle", {"center": v(-8, 34.4) * mm, "radius": 4.03 * mm, "construction": true});
            skLineSegment(sketch, "E52.0", {"start": v(-12.03, 36.72) * mm, "end": v(-8, 39.04) * mm});
            skLineSegment(sketch, "E52.1", {"start": v(-8, 39.04) * mm, "end": v(-3.97, 36.72) * mm});
            skLineSegment(sketch, "E52.2", {"start": v(-3.98, 36.72) * mm, "end": v(-3.98, 32.07) * mm});
            skLineSegment(sketch, "E52.3", {"start": v(-3.98, 32.07) * mm, "end": v(-8, 29.75) * mm});
            skLineSegment(sketch, "E52.4", {"start": v(-8, 29.75) * mm, "end": v(-12.02, 32.07) * mm});
            skLineSegment(sketch, "E52.5", {"start": v(-12.02, 32.07) * mm, "end": v(-12.02, 36.72) * mm});
            skPoint(sketch, "E52.0.midPoint", {"position": v(-10.01, 37.88) * mm});
            skSolve(sketch);
        }
        {
            var Q0;
            Q0=qSketchRegion(id+"F23",true);
            extrude(context, id + "F24", {"entities" : qUnion([Q0]), "operationType" : NewBodyOperationType.REMOVE, "oppositeDirection" : true, "depth" : 4 * mm});
        }
        {
            var Q0;
            Q0=makeQuery(id+"F3.opExtrude","SWEPT_FACE",FACE,{"disambiguationData":[OSD([sQuery(id+"F2.wireOp",EDGE,"E16.MirrorCS")])]});
            var sketch = newSketch(context, id + "F25", { "sketchPlane" : qUnion([Q0])});
            skCircle(sketch, "E53.cCircle", {"center": v(8, 34.4) * mm, "radius": 4.03 * mm, "construction": true});
            skLineSegment(sketch, "E53.0", {"start": v(12.02, 36.72) * mm, "end": v(12.02, 32.07) * mm});
            skLineSegment(sketch, "E53.1", {"start": v(12.03, 32.07) * mm, "end": v(8, 29.75) * mm});
            skLineSegment(sketch, "E53.2", {"start": v(8, 29.75) * mm, "end": v(3.98, 32.07) * mm});
            skLineSegment(sketch, "E53.3", {"start": v(3.98, 32.07) * mm, "end": v(3.98, 36.72) * mm});
            skLineSegment(sketch, "E53.4", {"start": v(3.98, 36.72) * mm, "end": v(8, 39.04) * mm});
            skLineSegment(sketch, "E53.5", {"start": v(8, 39.04) * mm, "end": v(12.03, 36.72) * mm});
            skPoint(sketch, "E53.0.midPoint", {"position": v(12.03, 34.4) * mm});
            skCircle(sketch, "E54.cCircle", {"center": v(8, 11.46) * mm, "radius": 4.03 * mm, "construction": true});
            skLineSegment(sketch, "E54.0", {"start": v(12.03, 13.79) * mm, "end": v(12.03, 9.14) * mm});
            skLineSegment(sketch, "E54.1", {"start": v(12.03, 9.14) * mm, "end": v(8, 6.82) * mm});
            skLineSegment(sketch, "E54.2", {"start": v(8, 6.82) * mm, "end": v(3.97, 9.14) * mm});
            skLineSegment(sketch, "E54.3", {"start": v(3.98, 9.14) * mm, "end": v(3.98, 13.79) * mm});
            skLineSegment(sketch, "E54.4", {"start": v(3.97, 13.79) * mm, "end": v(8, 16.11) * mm});
            skLineSegment(sketch, "E54.5", {"start": v(8, 16.11) * mm, "end": v(12.03, 13.79) * mm});
            skPoint(sketch, "E54.0.midPoint", {"position": v(12.03, 11.46) * mm});
            skSolve(sketch);
        }
        {
            var Q0;
            Q0=qSketchRegion(id+"F25",true);
            extrude(context, id + "F26", {"entities" : qUnion([Q0]), "operationType" : NewBodyOperationType.REMOVE, "oppositeDirection" : true, "depth" : 4 * mm});
        }
        {
            var Q0;
            Q0=makeQuery(id+"F3.opExtrude","SWEPT_FACE",FACE,{"disambiguationData":[OSD([sQuery(id+"F2.wireOp",EDGE,"E14")])]});
            var sketch = newSketch(context, id + "F27", { "sketchPlane" : qUnion([Q0])});
            skLineSegment(sketch, "E55", {"start": v(-4.15, 75.92) * mm, "end": v(-8.24, 73.05) * mm});
            skLineSegment(sketch, "E56", {"start": v(-5.95, 69.77) * mm, "end": v(-1.85, 72.64) * mm});
            skArc(sketch, "E57", {"start": v(-8.24, 73.05) * mm, "mid": v(-8.73, 70.26) * mm, "end": v(-5.95, 69.77) * mm});
            skArc(sketch, "E58", {"start": v(-1.85, 72.64) * mm, "mid": v(-1.36, 75.43) * mm, "end": v(-4.15, 75.92) * mm});
            skSolve(sketch);
        }
        {
            var Q0;
            Q0 = qSketchRegion(id + "F27", true);
            extrude(context, id + "F28", {"entities" : qUnion([Q0]), "operationType" : NewBodyOperationType.REMOVE, "endBound" : BoundingType.UP_TO_NEXT, "oppositeDirection" : true, "depth" : 25 * mm, "hasSecondDirection" : true, "secondDirectionOppositeDirection" : false, "secondDirectionDepth" : 15 * mm});
        }
        {
            var Q0;
            Q0=makeQuery(id+"F28.boolean.opBoolean","COPY",FACE,{"derivedFrom":makeQuery(id+"F28.opExtrude","CAP_FACE",FACE,{"disambiguationData":[OSD([sQuery(id+"F27.wireOp",EDGE,"E55"),sQuery(id+"F27.wireOp",EDGE,"E56"),sQuery(id+"F27.wireOp",EDGE,"E57"),sQuery(id+"F27.wireOp",EDGE,"E58")])],"isStart":true})});
            var sketch = newSketch(context, id + "F29", { "sketchPlane" : qUnion([Q0])});
            skCircle(sketch, "E59", {"center": v(3, 74.06) * mm, "radius": 4 * mm});
            skSolve(sketch);
        }
        {
            var Q0;
            Q0 = qSketchRegion(id + "F29", true);
            extrude(context, id + "F30", {"entities" : qUnion([Q0]), "operationType" : NewBodyOperationType.REMOVE, "depth" : 10 * mm});
        }
    });
